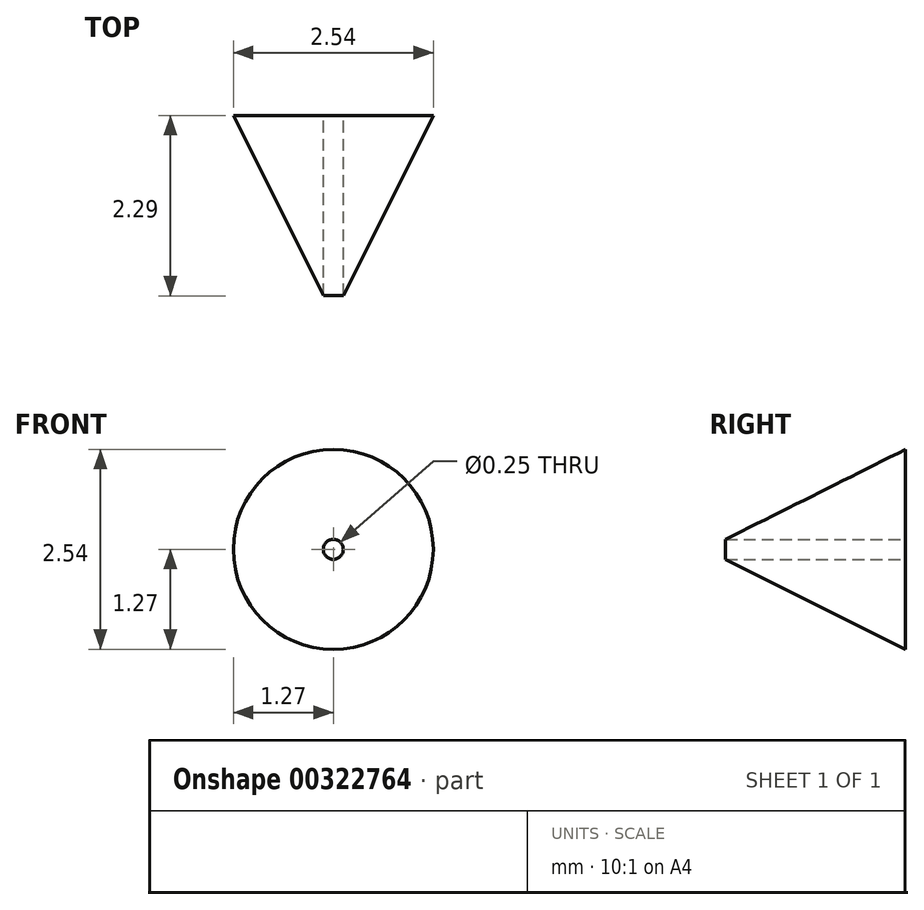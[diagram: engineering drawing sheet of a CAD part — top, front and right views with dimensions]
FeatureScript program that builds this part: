
annotation { "Feature Type Name" : "Feature", "Feature Type Description" : "" }
export const myFeature = defineFeature(function(context is Context, id is Id, definition is map)
    precondition{}
    {
        {
            var Q0;
            Q0=qCreatedBy(makeId("Front.planeOp"),FACE);
            var sketch = newSketch(context, id + "F0", { "sketchPlane" : qUnion([Q0])});
            skCircle(sketch, "E0", {"center": v(0, 0) * mm, "radius": 1.27 * mm});
            skSolve(sketch);
        }
        {
            var Q0;
            Q0 = qSketchRegion(id + "F0", true);
            extrude(context, id + "F1", {"entities" : qUnion([Q0]), "depth" : 2.54 * mm});
        }
        {
            var Q0;
            Q0=makeQuery(id+"F1.opExtrude","CAP_EDGE",EDGE,{"disambiguationData":[OSD([sQuery(id+"F0.wireOp",EDGE,"E0")])],"isStart":false});
            chamfer(context, id + "F2", {"entities" : qUnion([Q0]), "chamferType" : ChamferType.TWO_OFFSETS, "width1" : 1.27 * mm, "oppositeDirection" : false, "width2" : 2.54 * mm, "tangentPropagation" : true});
        }
        {
            var Q0;
            Q0=makeQuery(id+"F1.opExtrude","CAP_FACE",FACE,{"disambiguationData":[OSD([sQuery(id+"F0.wireOp",EDGE,"E0")])],"isStart":true});
            var sketch = newSketch(context, id + "F3", { "sketchPlane" : qUnion([Q0])});
            skCircle(sketch, "E1", {"center": v(0, 0) * mm, "radius": 0.13 * mm});
            skSolve(sketch);
        }
        {
            var Q0;
            Q0 = qSketchRegion(id + "F3", true);
            extrude(context, id + "F4", {"entities" : qUnion([Q0]), "operationType" : NewBodyOperationType.REMOVE, "endBound" : BoundingType.THROUGH_ALL, "oppositeDirection" : true, "depth" : 25.4 * mm});
        }
    });
